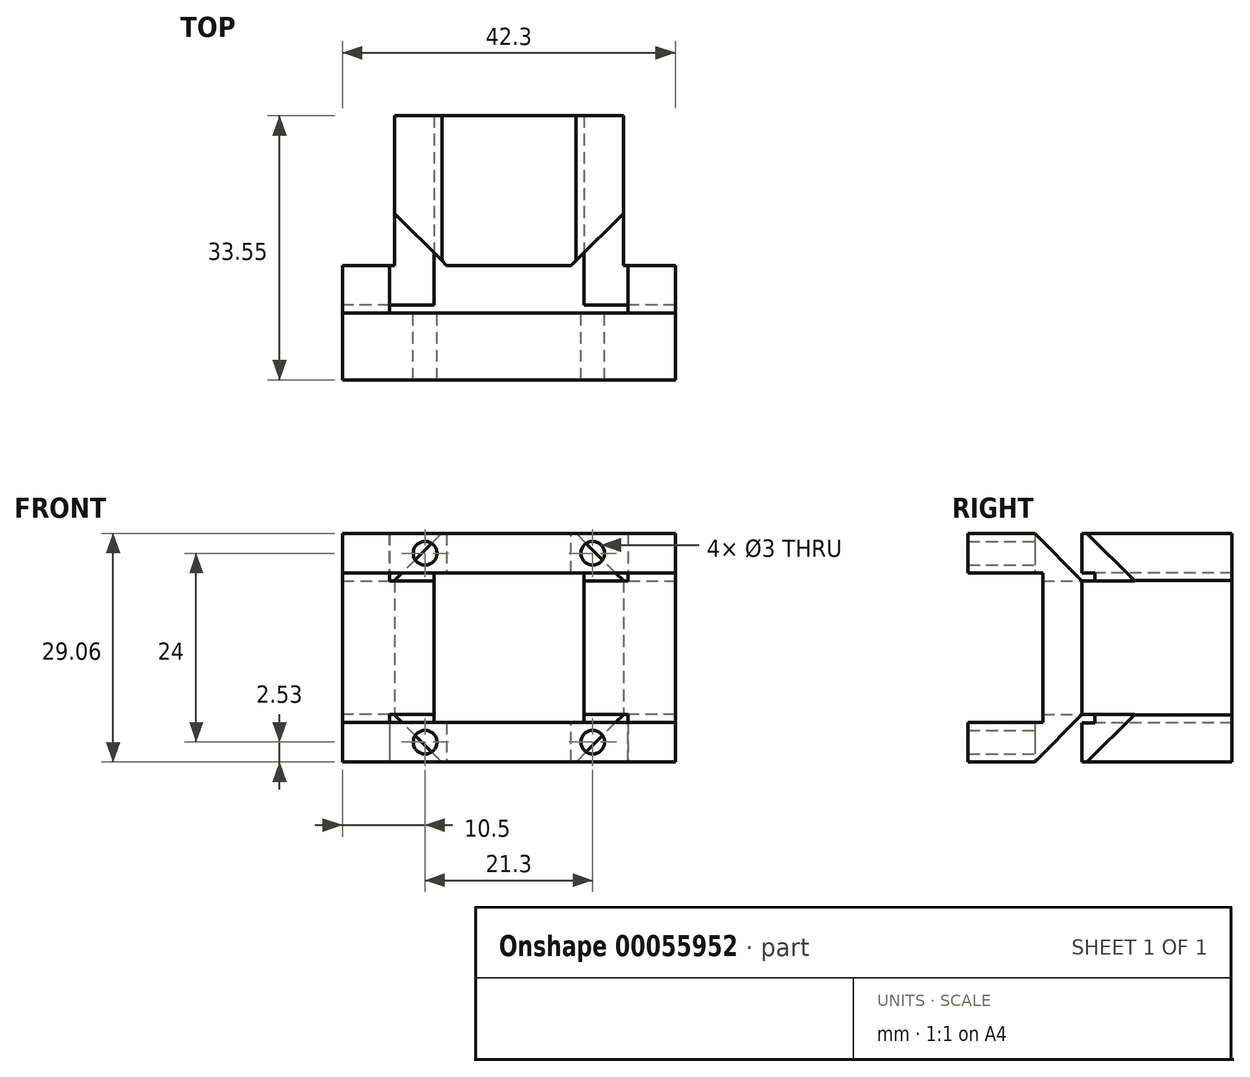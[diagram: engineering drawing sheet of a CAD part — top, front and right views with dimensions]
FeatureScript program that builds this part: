
annotation { "Feature Type Name" : "Feature", "Feature Type Description" : "" }
export const myFeature = defineFeature(function(context is Context, id is Id, definition is map)
    precondition{}
    {
        {
            var Q0;
            Q0=qCreatedBy(makeId("Right.planeOp"),FACE);
            var sketch = newSketch(context, id + "F0", { "sketchPlane" : qUnion([Q0])});
            skLineSegment(sketch, "E0.rect.bottom", {"start": v(9.5, 9.5) * mm, "end": v(0, 9.5) * mm});
            skLineSegment(sketch, "E0.rect.top", {"start": v(9.5, -9.5) * mm, "end": v(0, -9.5) * mm});
            skLineSegment(sketch, "E0.rect.left", {"start": v(9.5, 9.5) * mm, "end": v(9.5, -9.5) * mm});
            skPoint(sketch, "E0.rect.middle", {"position": v(0, 0) * mm});
            skLineSegment(sketch, "E1.rect.bottom", {"start": v(14.5, 14.5) * mm, "end": v(0, 14.5) * mm});
            skLineSegment(sketch, "E1.rect.top", {"start": v(14.5, -14.5) * mm, "end": v(0, -14.5) * mm});
            skLineSegment(sketch, "E1.rect.left", {"start": v(14.5, 14.5) * mm, "end": v(14.5, -14.5) * mm});
            skLineSegment(sketch, "E2", {"start": v(0, 9.5) * mm, "end": v(0, 14.5) * mm});
            skLineSegment(sketch, "E3", {"start": v(0, -9.5) * mm, "end": v(0, -14.5) * mm});
            skSolve(sketch);
        }
        {
            var Q0;
            Q0=makeQuery(id+"F0.imprint","IMPRINT",FACE,{"disambiguationData":[TD([[makeQuery(id+"F0.imprint","IMPRINT",EDGE,{"derivedFrom":sQuery(id+"F0.wireOp",EDGE,"5346ee42-6b44-4ab4-b06a-5ea702be0697.bottom")}),1.0]])]});
            var Q1;
            Q1=makeQuery(id+"F0.imprint","IMPRINT",FACE,{"disambiguationData":[TD([[makeQuery(id+"F0.imprint","IMPRINT",EDGE,{"derivedFrom":sQuery(id+"F0.wireOp",EDGE,"9599e187-f427-41b1-8912-62db417e26b9.bottom")}),1.0]])]});
            var Q2;
            Q2=makeQuery(id+"F0.imprint","IMPRINT",FACE,{"disambiguationData":[TD([[makeQuery(id+"F0.imprint","IMPRINT",EDGE,{"derivedFrom":sQuery(id+"F0.wireOp",EDGE,"E0.rect.bottom")}),-1.0]])]});
            extrude(context, id + "F1", {"entities" : qUnion([Q0, Q1, Q2]), "depth" : 42.3 * mm});
        }
        {
            var Q0;
            Q0=makeQuery(id+"F1.opExtrude","SWEPT_FACE",FACE,{"disambiguationData":[OSD([sQuery(id+"F0.wireOp",EDGE,"E1.rect.left")])]});
            var sketch = newSketch(context, id + "F2", { "sketchPlane" : qUnion([Q0])});
            skLineSegment(sketch, "E4.bottom", {"start": v(-42.3, 14.5) * mm, "end": v(-36.3, 14.5) * mm, "construction": true});
            skLineSegment(sketch, "E4.top", {"start": v(-42.3, 8.5) * mm, "end": v(-36.3, 8.5) * mm, "construction": true});
            skLineSegment(sketch, "E4.left", {"start": v(-42.3, 14.5) * mm, "end": v(-42.3, 8.5) * mm, "construction": true});
            skLineSegment(sketch, "E4.right", {"start": v(-36.3, 14.5) * mm, "end": v(-36.3, 8.5) * mm, "construction": true});
            skLineSegment(sketch, "E5.bottom", {"start": v(0, 14.5) * mm, "end": v(-6, 14.5) * mm, "construction": true});
            skLineSegment(sketch, "E5.top", {"start": v(0, 8.5) * mm, "end": v(-6, 8.5) * mm, "construction": true});
            skLineSegment(sketch, "E5.left", {"start": v(0, 14.5) * mm, "end": v(0, 8.5) * mm, "construction": true});
            skLineSegment(sketch, "E5.right", {"start": v(-6, 14.5) * mm, "end": v(-6, 8.5) * mm, "construction": true});
            skLineSegment(sketch, "E6.bottom", {"start": v(0, -14.5) * mm, "end": v(-6, -14.5) * mm, "construction": true});
            skLineSegment(sketch, "E6.top", {"start": v(0, -8.5) * mm, "end": v(-6, -8.5) * mm, "construction": true});
            skLineSegment(sketch, "E6.left", {"start": v(0, -14.5) * mm, "end": v(0, -8.5) * mm, "construction": true});
            skLineSegment(sketch, "E6.right", {"start": v(-6, -14.5) * mm, "end": v(-6, -8.5) * mm, "construction": true});
            skLineSegment(sketch, "E7.bottom", {"start": v(-42.3, -14.5) * mm, "end": v(-36.3, -14.5) * mm, "construction": true});
            skLineSegment(sketch, "E7.top", {"start": v(-42.3, -8.5) * mm, "end": v(-36.3, -8.5) * mm, "construction": true});
            skLineSegment(sketch, "E7.left", {"start": v(-42.3, -14.5) * mm, "end": v(-42.3, -8.5) * mm, "construction": true});
            skLineSegment(sketch, "E7.right", {"start": v(-36.3, -14.5) * mm, "end": v(-36.3, -8.5) * mm, "construction": true});
            skLineSegment(sketch, "E8.bottom", {"start": v(-36.3, 14.5) * mm, "end": v(-6, 14.5) * mm});
            skLineSegment(sketch, "E8.top", {"start": v(-36.3, 8.5) * mm, "end": v(-6, 8.5) * mm});
            skLineSegment(sketch, "E8.left", {"start": v(-36.3, 14.5) * mm, "end": v(-36.3, 8.5) * mm});
            skLineSegment(sketch, "E8.right", {"start": v(-6, 14.5) * mm, "end": v(-6, 8.5) * mm});
            skLineSegment(sketch, "E9.bottom", {"start": v(-36.3, -8.5) * mm, "end": v(-6, -8.5) * mm});
            skLineSegment(sketch, "E9.top", {"start": v(-36.3, -14.5) * mm, "end": v(-6, -14.5) * mm});
            skLineSegment(sketch, "E9.left", {"start": v(-36.3, -8.5) * mm, "end": v(-36.3, -14.5) * mm});
            skLineSegment(sketch, "E9.right", {"start": v(-6, -8.5) * mm, "end": v(-6, -14.5) * mm});
            skSolve(sketch);
        }
        {
            var Q0;
            Q0=makeQuery(id+"F2.imprint","IMPRINT",FACE,{"disambiguationData":[TD([[makeQuery(id+"F2.imprint","IMPRINT",EDGE,{"derivedFrom":sQuery(id+"F2.wireOp",EDGE,"E8.bottom")}),-1.0]])]});
            var Q1;
            Q1=makeQuery(id+"F2.imprint","IMPRINT",FACE,{"disambiguationData":[TD([[makeQuery(id+"F2.imprint","IMPRINT",EDGE,{"derivedFrom":sQuery(id+"F2.wireOp",EDGE,"E9.bottom")}),-1.0]])]});
            extrude(context, id + "F3", {"entities" : qUnion([Q0, Q1]), "operationType" : NewBodyOperationType.REMOVE, "oppositeDirection" : true, "depth" : 6 * mm});
        }
        {
            var Q0;
            {var subQ0=sQuery(id+"F0.wireOp",EDGE,"E1.rect.left");var subQ1=sQuery(id+"F0.wireOp",EDGE,"E1.rect.top");Q0=makeQuery(id+"F3.boolean.opBoolean","SPLIT",EDGE,{"disambiguationData":[TD([makeQuery(id+"F3.opExtrude","SWEPT_FACE",FACE,{"disambiguationData":[OSD([sQuery(id+"F2.wireOp",EDGE,"E9.right")])]})])],"derivedFrom":makeQuery(id+"F1.opExtrude","SWEPT_EDGE",EDGE,{"disambiguationData":[OSD([subQ1,subQ0])]})});}
            var Q1;
            {var subQ0=sQuery(id+"F0.wireOp",EDGE,"E1.rect.left");var subQ1=sQuery(id+"F0.wireOp",EDGE,"E1.rect.top");Q1=makeQuery(id+"F3.boolean.opBoolean","SPLIT",EDGE,{"disambiguationData":[TD([makeQuery(id+"F3.opExtrude","SWEPT_FACE",FACE,{"disambiguationData":[OSD([sQuery(id+"F2.wireOp",EDGE,"E9.left")])]})])],"derivedFrom":makeQuery(id+"F1.opExtrude","SWEPT_EDGE",EDGE,{"disambiguationData":[OSD([subQ1,subQ0])]})});}
            var Q2;
            {var subQ0=sQuery(id+"F0.wireOp",EDGE,"E1.rect.left");var subQ1=sQuery(id+"F0.wireOp",EDGE,"E1.rect.bottom");Q2=makeQuery(id+"F3.boolean.opBoolean","SPLIT",EDGE,{"disambiguationData":[TD([makeQuery(id+"F3.opExtrude","SWEPT_FACE",FACE,{"disambiguationData":[OSD([sQuery(id+"F2.wireOp",EDGE,"E8.left")])]})])],"derivedFrom":makeQuery(id+"F1.opExtrude","SWEPT_EDGE",EDGE,{"disambiguationData":[OSD([subQ1,subQ0])]})});}
            var Q3;
            {var subQ0=sQuery(id+"F0.wireOp",EDGE,"E1.rect.left");var subQ1=sQuery(id+"F0.wireOp",EDGE,"E1.rect.bottom");Q3=makeQuery(id+"F3.boolean.opBoolean","SPLIT",EDGE,{"disambiguationData":[TD([makeQuery(id+"F3.opExtrude","SWEPT_FACE",FACE,{"disambiguationData":[OSD([sQuery(id+"F2.wireOp",EDGE,"E8.right")])]})])],"derivedFrom":makeQuery(id+"F1.opExtrude","SWEPT_EDGE",EDGE,{"disambiguationData":[OSD([subQ1,subQ0])]})});}
            chamfer(context, id + "F4", {"entities" : qUnion([Q0, Q1, Q2, Q3]), "width" : 6 * mm, "tangentPropagation" : true});
        }
        {
            var Q0;
            Q0=makeQuery(id+"F3.boolean.opBoolean","COPY",FACE,{"derivedFrom":makeQuery(id+"F3.opExtrude","CAP_FACE",FACE,{"disambiguationData":[OSD([sQuery(id+"F2.wireOp",EDGE,"E8.bottom"),sQuery(id+"F2.wireOp",EDGE,"E8.top"),sQuery(id+"F2.wireOp",EDGE,"E8.left"),sQuery(id+"F2.wireOp",EDGE,"E8.right")])],"isStart":false})});
            var sketch = newSketch(context, id + "F5", { "sketchPlane" : qUnion([Q0])});
            skLineSegment(sketch, "E10", {"start": v(-36.3, 14.5) * mm, "end": v(-34.3, 14.5) * mm, "construction": true});
            skLineSegment(sketch, "E11", {"start": v(-34.3, 14.5) * mm, "end": v(-29.3, 14.5) * mm, "construction": true});
            skLineSegment(sketch, "E12", {"start": v(-29.3, 14.5) * mm, "end": v(-13, 14.5) * mm, "construction": true});
            skLineSegment(sketch, "E13", {"start": v(-13, 14.5) * mm, "end": v(-8, 14.5) * mm, "construction": true});
            skLineSegment(sketch, "E14", {"start": v(-8, 14.5) * mm, "end": v(-6, 14.5) * mm, "construction": true});
            skLineSegment(sketch, "E15", {"start": v(-34.3, 14.5) * mm, "end": v(-29.3, 9.5) * mm, "construction": true});
            skLineSegment(sketch, "E16", {"start": v(-13, 14.5) * mm, "end": v(-8, 9.5) * mm, "construction": true});
            skCircle(sketch, "E17", {"center": v(-31.8, 12) * mm, "radius": 1.5 * mm});
            skCircle(sketch, "E18", {"center": v(-10.5, 12) * mm, "radius": 1.5 * mm});
            skSolve(sketch);
        }
        {
            var Q0;
            Q0=makeQuery(id+"F5.imprint","IMPRINT",FACE,{"disambiguationData":[TD([[makeQuery(id+"F5.imprint","IMPRINT",EDGE,{"derivedFrom":sQuery(id+"F5.wireOp",EDGE,"E17")}),1.0]])]});
            var Q1;
            Q1=makeQuery(id+"F5.imprint","IMPRINT",FACE,{"disambiguationData":[TD([[makeQuery(id+"F5.imprint","IMPRINT",EDGE,{"derivedFrom":sQuery(id+"F5.wireOp",EDGE,"E18")}),1.0]])]});
            extrude(context, id + "F6", {"entities" : qUnion([Q0, Q1]), "operationType" : NewBodyOperationType.REMOVE, "endBound" : BoundingType.THROUGH_ALL, "oppositeDirection" : true, "depth" : 25 * mm});
        }
        {
            var Q0;
            Q0=makeQuery(id+"F3.boolean.opBoolean","COPY",FACE,{"derivedFrom":makeQuery(id+"F3.opExtrude","CAP_FACE",FACE,{"disambiguationData":[OSD([sQuery(id+"F2.wireOp",EDGE,"E9.bottom"),sQuery(id+"F2.wireOp",EDGE,"E9.top"),sQuery(id+"F2.wireOp",EDGE,"E9.left"),sQuery(id+"F2.wireOp",EDGE,"E9.right")])],"isStart":false})});
            var sketch = newSketch(context, id + "F7", { "sketchPlane" : qUnion([Q0])});
            skLineSegment(sketch, "E19", {"start": v(-36.3, -14.5) * mm, "end": v(-34.3, -14.5) * mm, "construction": true});
            skLineSegment(sketch, "E20", {"start": v(-34.3, -14.5) * mm, "end": v(-29.3, -14.5) * mm, "construction": true});
            skLineSegment(sketch, "E21", {"start": v(-29.3, -14.5) * mm, "end": v(-13, -14.5) * mm, "construction": true});
            skLineSegment(sketch, "E22", {"start": v(-13, -14.5) * mm, "end": v(-8, -14.5) * mm, "construction": true});
            skLineSegment(sketch, "E23", {"start": v(-8, -14.5) * mm, "end": v(-6, -14.5) * mm, "construction": true});
            skLineSegment(sketch, "E24", {"start": v(-34.3, -14.5) * mm, "end": v(-29.3, -9.5) * mm, "construction": true});
            skLineSegment(sketch, "E25", {"start": v(-13, -14.5) * mm, "end": v(-8, -9.5) * mm, "construction": true});
            skCircle(sketch, "E26", {"center": v(-31.8, -12) * mm, "radius": 1.5 * mm});
            skCircle(sketch, "E27", {"center": v(-10.5, -12) * mm, "radius": 1.5 * mm});
            skSolve(sketch);
        }
        {
            var Q0;
            Q0=makeQuery(id+"F7.imprint","IMPRINT",FACE,{"disambiguationData":[TD([[makeQuery(id+"F7.imprint","IMPRINT",EDGE,{"derivedFrom":sQuery(id+"F7.wireOp",EDGE,"E26")}),1.0]])]});
            var Q1;
            Q1=makeQuery(id+"F7.imprint","IMPRINT",FACE,{"disambiguationData":[TD([[makeQuery(id+"F7.imprint","IMPRINT",EDGE,{"derivedFrom":sQuery(id+"F7.wireOp",EDGE,"E27")}),1.0]])]});
            extrude(context, id + "F8", {"entities" : qUnion([Q0, Q1]), "operationType" : NewBodyOperationType.REMOVE, "endBound" : BoundingType.THROUGH_ALL, "oppositeDirection" : true, "depth" : 25 * mm});
        }
        {
            var Q0;
            Q0=makeQuery(id+"F1.opExtrude","SWEPT_FACE",FACE,{"disambiguationData":[OSD([sQuery(id+"F0.wireOp",EDGE,"E1.rect.left")])]});
            var sketch = newSketch(context, id + "F9", { "sketchPlane" : qUnion([Q0])});
            skLineSegment(sketch, "E28", {"start": v(-21.15, 9.5) * mm, "end": v(-21.15, -9.5) * mm, "construction": true});
            skLineSegment(sketch, "E29.rect.bottom", {"start": v(-11.62, 9.53) * mm, "end": v(-30.67, 9.53) * mm});
            skLineSegment(sketch, "E29.rect.top", {"start": v(-11.62, -9.52) * mm, "end": v(-30.67, -9.52) * mm});
            skLineSegment(sketch, "E29.rect.left", {"start": v(-11.62, 9.53) * mm, "end": v(-11.62, -9.52) * mm});
            skLineSegment(sketch, "E29.rect.right", {"start": v(-30.67, 9.53) * mm, "end": v(-30.67, -9.52) * mm});
            skPoint(sketch, "E29.rect.middle", {"position": v(-21.15, 0) * mm});
            skLineSegment(sketch, "E30.rect.bottom", {"start": v(-6.62, 14.53) * mm, "end": v(-35.67, 14.53) * mm});
            skLineSegment(sketch, "E30.rect.top", {"start": v(-6.62, -14.52) * mm, "end": v(-35.67, -14.52) * mm});
            skLineSegment(sketch, "E30.rect.left", {"start": v(-6.62, 14.53) * mm, "end": v(-6.62, -14.52) * mm});
            skLineSegment(sketch, "E30.rect.right", {"start": v(-35.67, 14.53) * mm, "end": v(-35.67, -14.53) * mm});
            skSolve(sketch);
        }
        {
            var Q0;
            {var subQ0=sQuery(id+"F9.wireOp",EDGE,"E29.rect.right");var subQ1=makeQuery(id+"F3.boolean.opBoolean","COPY",EDGE,{"derivedFrom":makeQuery(id+"F3.opExtrude","CAP_EDGE",EDGE,{"disambiguationData":[OSD([sQuery(id+"F2.wireOp",EDGE,"E8.top")])],"isStart":true})});var subQ2=makeQuery(id+"F9.imprint","INTERSECT",VERTEX,{"derivedFrom":[subQ1,subQ0]});Q0=makeQuery(id+"F9.imprint","IMPRINT",FACE,{"disambiguationData":[TD([[makeQuery(id+"F9.imprint","IMPRINT",EDGE,{"disambiguationData":[TD([[subQ2,-1.0]])],"derivedFrom":subQ0}),-1.0]])]});}
            var Q1;
            {var subQ0=sQuery(id+"F9.wireOp",EDGE,"E29.rect.left");var subQ1=makeQuery(id+"F3.boolean.opBoolean","COPY",EDGE,{"derivedFrom":makeQuery(id+"F3.opExtrude","CAP_EDGE",EDGE,{"disambiguationData":[OSD([sQuery(id+"F2.wireOp",EDGE,"E8.top")])],"isStart":true})});var subQ2=makeQuery(id+"F9.imprint","INTERSECT",VERTEX,{"derivedFrom":[subQ1,subQ0]});Q1=makeQuery(id+"F9.imprint","IMPRINT",FACE,{"disambiguationData":[TD([[makeQuery(id+"F9.imprint","IMPRINT",EDGE,{"disambiguationData":[TD([[subQ2,-1.0]])],"derivedFrom":subQ0}),1.0]])]});}
            var Q2;
            {var subQ1=sQuery(id+"F9.wireOp",EDGE,"E29.rect.bottom");Q2=makeQuery(id+"F9.imprint","IMPRINT",FACE,{"disambiguationData":[TD([[makeQuery(id+"F9.imprint","IMPRINT",EDGE,{"derivedFrom":subQ1}),-1.0]])]});}
            var Q3;
            {var subQ1=sQuery(id+"F9.wireOp",EDGE,"E29.rect.top");Q3=makeQuery(id+"F9.imprint","IMPRINT",FACE,{"disambiguationData":[TD([[makeQuery(id+"F9.imprint","IMPRINT",EDGE,{"derivedFrom":subQ1}),1.0]])]});}
            extrude(context, id + "F10", {"entities" : qUnion([Q0, Q1, Q2, Q3]), "operationType" : NewBodyOperationType.ADD, "depth" : 19.05 * mm});
        }
        {
            var Q0;
            {var subQ1=sQuery(id+"F9.wireOp",EDGE,"E29.rect.left");Q0=makeQuery(id+"F10.boolean.opBoolean","SPLIT",FACE,{"disambiguationData":[TD([makeQuery(id+"F10.opExtrude","SWEPT_FACE",FACE,{"disambiguationData":[OSD([subQ1])]})])],"derivedFrom":makeQuery(id+"F1.opExtrude","SWEPT_FACE",FACE,{"disambiguationData":[OSD([sQuery(id+"F0.wireOp",EDGE,"E1.rect.left")])]})});}
            extrude(context, id + "F11", {"entities" : qUnion([Q0]), "operationType" : NewBodyOperationType.REMOVE, "endBound" : BoundingType.UP_TO_NEXT, "oppositeDirection" : true, "depth" : 25 * mm});
        }
        {
            var Q0;
            {var subQ0=sQuery(id+"F9.wireOp",EDGE,"E30.rect.right");Q0=makeQuery(id+"F10.boolean.opBoolean","SPLIT",EDGE,{"disambiguationData":[topologyDisambiguationEdgeConnected([makeQuery(id+"F1.opExtrude","SWEPT_FACE",FACE,{"disambiguationData":[OSD([sQuery(id+"F0.wireOp",EDGE,"E1.rect.left")])]}),makeQuery(id+"F10.opExtrude","SWEPT_FACE",FACE,{"disambiguationData":[OSD([subQ0])]})])],"derivedFrom":makeQuery(id+"F10.opExtrude","CAP_EDGE",EDGE,{"disambiguationData":[OSD([subQ0])],"isStart":true})});}
            var Q1;
            {var subQ0=sQuery(id+"F9.wireOp",EDGE,"E30.rect.left");Q1=makeQuery(id+"F10.boolean.opBoolean","SPLIT",EDGE,{"disambiguationData":[topologyDisambiguationEdgeConnected([makeQuery(id+"F1.opExtrude","SWEPT_FACE",FACE,{"disambiguationData":[OSD([sQuery(id+"F0.wireOp",EDGE,"E1.rect.left")])]}),makeQuery(id+"F10.opExtrude","SWEPT_FACE",FACE,{"disambiguationData":[OSD([subQ0])]})])],"derivedFrom":makeQuery(id+"F10.opExtrude","CAP_EDGE",EDGE,{"disambiguationData":[OSD([subQ0])],"isStart":true})});}
            chamfer(context, id + "F12", {"entities" : qUnion([Q0, Q1]), "width" : 6.62 * mm, "tangentPropagation" : true});
        }
        {
            var Q0;
            Q0=makeQuery(id+"F10.opExtrude","SWEPT_EDGE",EDGE,{"disambiguationData":[OSD([sQuery(id+"F9.wireOp",EDGE,"E30.rect.bottom"),sQuery(id+"F9.wireOp",EDGE,"E30.rect.left")])]});
            var Q1;
            Q1=makeQuery(id+"F10.opExtrude","SWEPT_EDGE",EDGE,{"disambiguationData":[OSD([sQuery(id+"F9.wireOp",EDGE,"E30.rect.bottom"),sQuery(id+"F9.wireOp",EDGE,"E30.rect.right")])]});
            var Q2;
            Q2=makeQuery(id+"F10.opExtrude","SWEPT_EDGE",EDGE,{"disambiguationData":[OSD([sQuery(id+"F9.wireOp",EDGE,"E30.rect.top"),sQuery(id+"F9.wireOp",EDGE,"E30.rect.right")])]});
            var Q3;
            Q3=makeQuery(id+"F10.opExtrude","SWEPT_EDGE",EDGE,{"disambiguationData":[OSD([sQuery(id+"F9.wireOp",EDGE,"E30.rect.top"),sQuery(id+"F9.wireOp",EDGE,"E30.rect.left")])]});
            chamfer(context, id + "F13", {"entities" : qUnion([Q0, Q1, Q2, Q3]), "width" : 6 * mm, "tangentPropagation" : true});
        }
        {
            var Q0;
            Q0=makeQuery(id+"F1.opExtrude","SWEPT_FACE",FACE,{"disambiguationData":[OSD([sQuery(id+"F0.wireOp",EDGE,"E0.rect.top")])]});
            var sketch = newSketch(context, id + "F14", { "sketchPlane" : qUnion([Q0])});
            skLineSegment(sketch, "E31", {"start": v(6, 9.5) * mm, "end": v(36.3, 9.5) * mm, "construction": true});
            skSolve(sketch);
        }
    });
